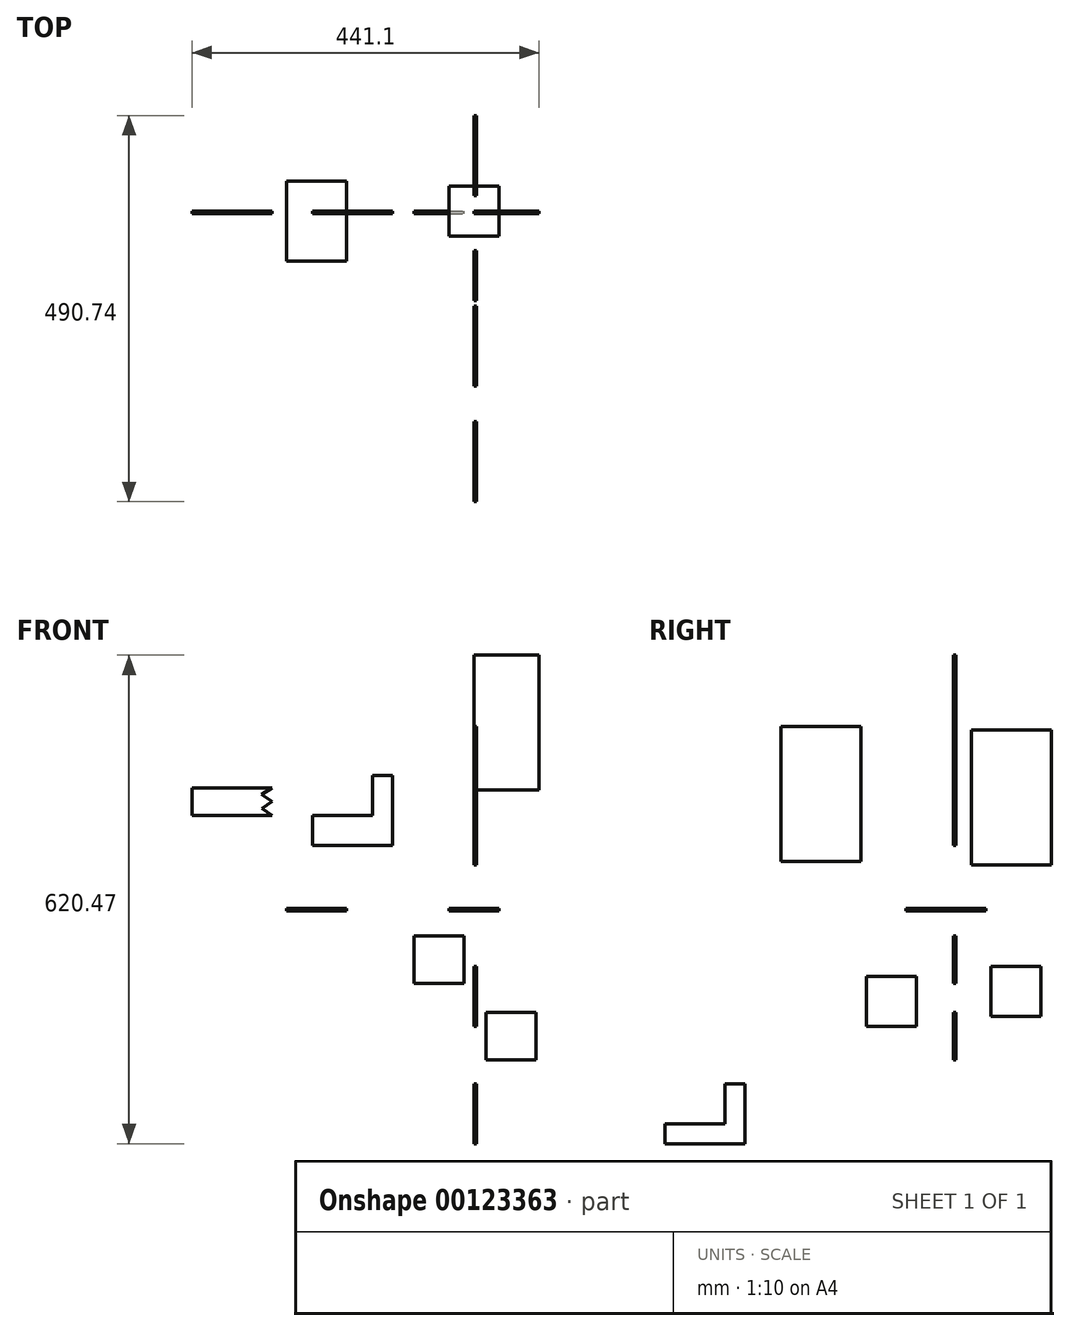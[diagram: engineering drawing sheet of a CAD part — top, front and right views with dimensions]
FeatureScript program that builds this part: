
annotation { "Feature Type Name" : "Feature", "Feature Type Description" : "" }
export const myFeature = defineFeature(function(context is Context, id is Id, definition is map)
    precondition{}
    {
        {
            var Q0;
            Q0=qCreatedBy(makeId("Top.planeOp"),FACE);
            var sketch = newSketch(context, id + "F0", { "sketchPlane" : qUnion([Q0])});
            skLineSegment(sketch, "E0.bottom", {"start": v(31.75, 31.75) * mm, "end": v(-31.75, 31.75) * mm});
            skLineSegment(sketch, "E0.top", {"start": v(31.75, -31.75) * mm, "end": v(-31.75, -31.75) * mm});
            skLineSegment(sketch, "E0.left", {"start": v(31.75, 31.75) * mm, "end": v(31.75, -31.75) * mm});
            skLineSegment(sketch, "E0.right", {"start": v(-31.75, 31.75) * mm, "end": v(-31.75, -31.75) * mm});
            skPoint(sketch, "E0.middle", {"position": v(0, 0) * mm});
            skLineSegment(sketch, "E1.bottom", {"start": v(-170.84, 127.02) * mm, "end": v(3.78, 127.02) * mm});
            skLineSegment(sketch, "E1.top", {"start": v(-170.84, 228.62) * mm, "end": v(3.78, 228.62) * mm});
            skLineSegment(sketch, "E1.left", {"start": v(-170.84, 127.02) * mm, "end": v(-170.84, 228.62) * mm});
            skLineSegment(sketch, "E1.right", {"start": v(3.78, 127.02) * mm, "end": v(3.78, 228.62) * mm});
            skPoint(sketch, "E1.middle", {"position": v(-83.53, 177.82) * mm});
            skLineSegment(sketch, "E2.bottom", {"start": v(0, -294.23) * mm, "end": v(-174.62, -294.23) * mm});
            skLineSegment(sketch, "E2.top", {"start": v(0, -192.63) * mm, "end": v(-174.63, -192.63) * mm});
            skLineSegment(sketch, "E2.left", {"start": v(0, -294.23) * mm, "end": v(0, -192.63) * mm});
            skLineSegment(sketch, "E2.right", {"start": v(-174.62, -294.23) * mm, "end": v(-174.63, -192.63) * mm});
            skPoint(sketch, "E2.middle", {"position": v(-87.31, -243.43) * mm});
            skLineSegment(sketch, "E3.bottom", {"start": v(-238.6, -63.17) * mm, "end": v(-162.4, -63.17) * mm});
            skLineSegment(sketch, "E3.top", {"start": v(-238.6, 38.43) * mm, "end": v(-162.4, 38.43) * mm});
            skLineSegment(sketch, "E3.left", {"start": v(-238.6, -63.17) * mm, "end": v(-238.6, 38.43) * mm});
            skLineSegment(sketch, "E3.right", {"start": v(-162.4, -63.17) * mm, "end": v(-162.4, 38.43) * mm});
            skPoint(sketch, "E3.middle", {"position": v(-200.5, -12.37) * mm});
            skSolve(sketch);
        }
        {
            var Q0;
            Q0=makeQuery(id+"F0.imprint","IMPRINT",FACE,{"disambiguationData":[TD([[makeQuery(id+"F0.imprint","IMPRINT",EDGE,{"derivedFrom":sQuery(id+"F0.wireOp",EDGE,"E0.bottom")}),1.0]])]});
            extrude(context, id + "F1", {"entities" : qUnion([Q0]), "depth" : 3.17 * mm});
        }
        {
            var Q0;
            Q0=qCreatedBy(makeId("Front.planeOp"),FACE);
            var sketch = newSketch(context, id + "F2", { "sketchPlane" : qUnion([Q0])});
            skLineSegment(sketch, "E4.bottom", {"start": v(-76.17, -31.8) * mm, "end": v(-12.67, -31.8) * mm});
            skLineSegment(sketch, "E4.top", {"start": v(-76.17, -92.13) * mm, "end": v(-12.67, -92.13) * mm});
            skLineSegment(sketch, "E4.left", {"start": v(-76.17, -31.8) * mm, "end": v(-76.17, -92.13) * mm});
            skLineSegment(sketch, "E4.right", {"start": v(-12.67, -31.8) * mm, "end": v(-12.67, -92.13) * mm});
            skPoint(sketch, "E4.middle", {"position": v(-44.42, -61.96) * mm});
            skLineSegment(sketch, "E5.bottom", {"start": v(14.92, -128.65) * mm, "end": v(78.42, -128.65) * mm});
            skLineSegment(sketch, "E5.top", {"start": v(14.92, -188.98) * mm, "end": v(78.42, -188.98) * mm});
            skLineSegment(sketch, "E5.left", {"start": v(14.92, -128.65) * mm, "end": v(14.92, -188.98) * mm});
            skLineSegment(sketch, "E5.right", {"start": v(78.42, -128.65) * mm, "end": v(78.42, -188.98) * mm});
            skPoint(sketch, "E5.middle", {"position": v(46.67, -158.82) * mm});
            skLineSegment(sketch, "E6.bottom", {"start": v(0, 324.95) * mm, "end": v(82.55, 324.95) * mm});
            skLineSegment(sketch, "E6.top", {"start": v(0, 153.5) * mm, "end": v(82.55, 153.5) * mm});
            skLineSegment(sketch, "E6.left", {"start": v(0, 324.95) * mm, "end": v(0, 153.5) * mm});
            skLineSegment(sketch, "E6.right", {"start": v(82.55, 324.95) * mm, "end": v(82.55, 153.5) * mm});
            skPoint(sketch, "E6.middle", {"position": v(41.28, 239.22) * mm});
            skLineSegment(sketch, "E7.bottom", {"start": v(-170.31, 227.53) * mm, "end": v(-271.91, 227.53) * mm});
            skLineSegment(sketch, "E7.top", {"start": v(-170.31, 265.63) * mm, "end": v(-271.91, 265.63) * mm});
            skLineSegment(sketch, "E7.left", {"start": v(-170.31, 227.53) * mm, "end": v(-170.31, 265.63) * mm});
            skLineSegment(sketch, "E7.right", {"start": v(-271.91, 227.53) * mm, "end": v(-271.91, 265.63) * mm});
            skPoint(sketch, "E7.middle", {"position": v(-221.11, 246.58) * mm});
            skLineSegment(sketch, "E8.bottom", {"start": v(-271.91, 227.53) * mm, "end": v(-246.51, 227.53) * mm});
            skLineSegment(sketch, "E8.top", {"start": v(-271.91, 316.43) * mm, "end": v(-246.51, 316.43) * mm});
            skLineSegment(sketch, "E8.left", {"start": v(-271.91, 227.53) * mm, "end": v(-271.91, 316.43) * mm});
            skLineSegment(sketch, "E8.right", {"start": v(-246.51, 227.53) * mm, "end": v(-246.51, 316.43) * mm});
            skLineSegment(sketch, "E9.bottom", {"start": v(-205.58, 121.73) * mm, "end": v(-103.98, 121.73) * mm});
            skLineSegment(sketch, "E9.top", {"start": v(-205.58, 83.63) * mm, "end": v(-103.98, 83.63) * mm});
            skLineSegment(sketch, "E9.left", {"start": v(-205.58, 121.73) * mm, "end": v(-205.58, 83.63) * mm});
            skLineSegment(sketch, "E9.right", {"start": v(-103.98, 121.73) * mm, "end": v(-103.98, 83.63) * mm});
            skPoint(sketch, "E9.middle", {"position": v(-154.78, 102.68) * mm});
            skLineSegment(sketch, "E10.bottom", {"start": v(-103.98, 83.63) * mm, "end": v(-129.38, 83.63) * mm});
            skLineSegment(sketch, "E10.top", {"start": v(-103.98, 172.53) * mm, "end": v(-129.38, 172.53) * mm});
            skLineSegment(sketch, "E10.left", {"start": v(-103.98, 83.63) * mm, "end": v(-103.98, 172.53) * mm});
            skLineSegment(sketch, "E10.right", {"start": v(-129.38, 83.63) * mm, "end": v(-129.38, 172.53) * mm});
            skLineSegment(sketch, "E11.bottom", {"start": v(-358.55, 156.27) * mm, "end": v(-256.95, 156.27) * mm});
            skLineSegment(sketch, "E11.top", {"start": v(-358.55, 121.7) * mm, "end": v(-256.95, 121.7) * mm});
            skLineSegment(sketch, "E11.left", {"start": v(-358.55, 156.27) * mm, "end": v(-358.55, 121.7) * mm});
            skLineSegment(sketch, "E11.right", {"start": v(-256.95, 156.27) * mm, "end": v(-256.95, 121.7) * mm});
            skPoint(sketch, "E11.middle", {"position": v(-307.75, 138.99) * mm});
            skLineSegment(sketch, "E12", {"start": v(-256.95, 121.7) * mm, "end": v(-269.2, 130.33) * mm});
            skLineSegment(sketch, "E13", {"start": v(-269.2, 130.33) * mm, "end": v(-256.95, 138.99) * mm});
            skLineSegment(sketch, "E14", {"start": v(-256.95, 138.99) * mm, "end": v(-269.2, 130.33) * mm});
            skLineSegment(sketch, "E15", {"start": v(-256.95, 156.27) * mm, "end": v(-270.41, 148.14) * mm});
            skLineSegment(sketch, "E16", {"start": v(-270.41, 148.14) * mm, "end": v(-256.95, 138.99) * mm});
            skSolve(sketch);
        }
        {
            var Q0;
            Q0=makeQuery(id+"F2.imprint","IMPRINT",FACE,{"disambiguationData":[TD([[makeQuery(id+"F2.imprint","IMPRINT",EDGE,{"derivedFrom":sQuery(id+"F2.wireOp",EDGE,"E4.bottom")}),-1.0]])]});
            extrude(context, id + "F3", {"entities" : qUnion([Q0]), "depth" : 3.17 * mm});
        }
        {
            var Q0;
            Q0=makeQuery(id+"F2.imprint","IMPRINT",FACE,{"disambiguationData":[TD([[makeQuery(id+"F2.imprint","IMPRINT",EDGE,{"derivedFrom":sQuery(id+"F2.wireOp",EDGE,"E5.bottom")}),-1.0]])]});
            extrude(context, id + "F4", {"entities" : qUnion([Q0]), "depth" : 3.17 * mm});
        }
        {
            var Q0;
            Q0=qCreatedBy(makeId("Right.planeOp"),FACE);
            var sketch = newSketch(context, id + "F5", { "sketchPlane" : qUnion([Q0])});
            skLineSegment(sketch, "E17.bottom", {"start": v(108.43, -133.8) * mm, "end": v(44.93, -133.8) * mm});
            skLineSegment(sketch, "E17.top", {"start": v(108.43, -70.3) * mm, "end": v(44.93, -70.3) * mm});
            skLineSegment(sketch, "E17.left", {"start": v(108.43, -133.8) * mm, "end": v(108.43, -70.3) * mm});
            skLineSegment(sketch, "E17.right", {"start": v(44.93, -133.8) * mm, "end": v(44.93, -70.3) * mm});
            skPoint(sketch, "E17.middle", {"position": v(76.68, -102.05) * mm});
            skLineSegment(sketch, "E18.bottom", {"start": v(-50.17, -146.33) * mm, "end": v(-113.67, -146.33) * mm});
            skLineSegment(sketch, "E18.top", {"start": v(-50.17, -82.83) * mm, "end": v(-113.67, -82.83) * mm});
            skLineSegment(sketch, "E18.left", {"start": v(-50.17, -146.33) * mm, "end": v(-50.17, -82.83) * mm});
            skLineSegment(sketch, "E18.right", {"start": v(-113.67, -146.33) * mm, "end": v(-113.67, -82.83) * mm});
            skPoint(sketch, "E18.middle", {"position": v(-81.92, -114.58) * mm});
            skLineSegment(sketch, "E19.bottom", {"start": v(-120.5, 234.76) * mm, "end": v(-222.1, 234.76) * mm});
            skLineSegment(sketch, "E19.top", {"start": v(-120.5, 63.3) * mm, "end": v(-222.1, 63.3) * mm});
            skLineSegment(sketch, "E19.left", {"start": v(-120.5, 234.76) * mm, "end": v(-120.5, 63.3) * mm});
            skLineSegment(sketch, "E19.right", {"start": v(-222.1, 234.76) * mm, "end": v(-222.1, 63.3) * mm});
            skPoint(sketch, "E19.middle", {"position": v(-171.3, 149.03) * mm});
            skLineSegment(sketch, "E20.bottom", {"start": v(121.62, 230.13) * mm, "end": v(20.02, 230.13) * mm});
            skLineSegment(sketch, "E20.top", {"start": v(121.62, 58.68) * mm, "end": v(20.02, 58.68) * mm});
            skLineSegment(sketch, "E20.left", {"start": v(121.62, 230.13) * mm, "end": v(121.62, 58.68) * mm});
            skLineSegment(sketch, "E20.right", {"start": v(20.02, 230.13) * mm, "end": v(20.02, 58.68) * mm});
            skPoint(sketch, "E20.middle", {"position": v(70.82, 144.4) * mm});
            skLineSegment(sketch, "E21.bottom", {"start": v(-402.14, -117.24) * mm, "end": v(-300.54, -117.24) * mm});
            skLineSegment(sketch, "E21.top", {"start": v(-402.14, -142.64) * mm, "end": v(-300.54, -142.64) * mm});
            skLineSegment(sketch, "E21.left", {"start": v(-402.14, -117.24) * mm, "end": v(-402.14, -142.64) * mm});
            skLineSegment(sketch, "E21.right", {"start": v(-300.54, -117.24) * mm, "end": v(-300.54, -142.64) * mm});
            skPoint(sketch, "E21.middle", {"position": v(-351.34, -129.94) * mm});
            skLineSegment(sketch, "E22.bottom", {"start": v(-369.12, -270.12) * mm, "end": v(-267.52, -270.12) * mm});
            skLineSegment(sketch, "E22.top", {"start": v(-369.12, -295.52) * mm, "end": v(-267.52, -295.52) * mm});
            skLineSegment(sketch, "E22.left", {"start": v(-369.12, -270.12) * mm, "end": v(-369.12, -295.52) * mm});
            skLineSegment(sketch, "E22.right", {"start": v(-267.52, -270.12) * mm, "end": v(-267.52, -295.52) * mm});
            skPoint(sketch, "E22.middle", {"position": v(-318.32, -282.82) * mm});
            skLineSegment(sketch, "E23.bottom", {"start": v(-267.52, -295.52) * mm, "end": v(-292.92, -295.52) * mm});
            skLineSegment(sketch, "E23.top", {"start": v(-267.52, -219.32) * mm, "end": v(-292.92, -219.32) * mm});
            skLineSegment(sketch, "E23.left", {"start": v(-267.52, -295.52) * mm, "end": v(-267.52, -219.32) * mm});
            skLineSegment(sketch, "E23.right", {"start": v(-292.92, -295.52) * mm, "end": v(-292.92, -219.32) * mm});
            skSolve(sketch);
        }
        {
            var Q0;
            Q0=makeQuery(id+"F5.imprint","IMPRINT",FACE,{"disambiguationData":[TD([[makeQuery(id+"F5.imprint","IMPRINT",EDGE,{"derivedFrom":sQuery(id+"F5.wireOp",EDGE,"E18.bottom")}),-1.0]])]});
            var Q1;
            Q1=makeQuery(id+"F5.imprint","IMPRINT",FACE,{"disambiguationData":[TD([[makeQuery(id+"F5.imprint","IMPRINT",EDGE,{"derivedFrom":sQuery(id+"F5.wireOp",EDGE,"E17.bottom")}),-1.0]])]});
            extrude(context, id + "F6", {"entities" : qUnion([Q0, Q1]), "depth" : 3.17 * mm});
        }
        {
            var Q0;
            Q0=makeQuery(id+"F0.imprint","IMPRINT",FACE,{"disambiguationData":[TD([[makeQuery(id+"F0.imprint","IMPRINT",EDGE,{"derivedFrom":sQuery(id+"F0.wireOp",EDGE,"E3.bottom")}),1.0]])]});
            extrude(context, id + "F7", {"entities" : qUnion([Q0]), "depth" : 3.17 * mm});
        }
        {
            var Q0;
            Q0=makeQuery(id+"F5.imprint","IMPRINT",FACE,{"disambiguationData":[TD([[makeQuery(id+"F5.imprint","IMPRINT",EDGE,{"derivedFrom":sQuery(id+"F5.wireOp",EDGE,"E20.bottom")}),1.0]])]});
            extrude(context, id + "F8", {"entities" : qUnion([Q0]), "depth" : 3.17 * mm});
        }
        {
            var Q0;
            Q0=makeQuery(id+"F5.imprint","IMPRINT",FACE,{"disambiguationData":[TD([[makeQuery(id+"F5.imprint","IMPRINT",EDGE,{"derivedFrom":sQuery(id+"F5.wireOp",EDGE,"E19.bottom")}),1.0]])]});
            extrude(context, id + "F9", {"entities" : qUnion([Q0]), "depth" : 3.17 * mm});
        }
        {
            var Q0;
            Q0=makeQuery(id+"F2.imprint","IMPRINT",FACE,{"disambiguationData":[TD([[makeQuery(id+"F2.imprint","IMPRINT",EDGE,{"derivedFrom":sQuery(id+"F2.wireOp",EDGE,"E6.bottom")}),-1.0]])]});
            extrude(context, id + "F10", {"entities" : qUnion([Q0]), "depth" : 3.17 * mm});
        }
        {
            var Q0;
            {var subQ4=sQuery(id+"F5.wireOp",EDGE,"E22.top");Q0=makeQuery(id+"F5.imprint","IMPRINT",FACE,{"disambiguationData":[TD([[makeQuery(id+"F5.imprint","IMPRINT",EDGE,{"derivedFrom":subQ4}),1.0]])]});}
            var Q1;
            {var subQ5=sQuery(id+"F5.wireOp",EDGE,"E23.bottom");Q1=makeQuery(id+"F5.imprint","IMPRINT",FACE,{"disambiguationData":[TD([[makeQuery(id+"F5.imprint","IMPRINT",EDGE,{"derivedFrom":subQ5}),-1.0]])]});}
            var Q2;
            {var subQ5=sQuery(id+"F5.wireOp",EDGE,"E23.top");Q2=makeQuery(id+"F5.imprint","IMPRINT",FACE,{"disambiguationData":[TD([[makeQuery(id+"F5.imprint","IMPRINT",EDGE,{"derivedFrom":subQ5}),1.0]])]});}
            extrude(context, id + "F11", {"entities" : qUnion([Q0, Q1, Q2]), "depth" : 3.17 * mm});
        }
        {
            var Q0;
            {var subQ5=sQuery(id+"F2.wireOp",EDGE,"E10.top");Q0=makeQuery(id+"F2.imprint","IMPRINT",FACE,{"disambiguationData":[TD([[makeQuery(id+"F2.imprint","IMPRINT",EDGE,{"derivedFrom":subQ5}),1.0]])]});}
            var Q1;
            {var subQ5=sQuery(id+"F2.wireOp",EDGE,"E10.bottom");Q1=makeQuery(id+"F2.imprint","IMPRINT",FACE,{"disambiguationData":[TD([[makeQuery(id+"F2.imprint","IMPRINT",EDGE,{"derivedFrom":subQ5}),-1.0]])]});}
            var Q2;
            {var subQ4=sQuery(id+"F2.wireOp",EDGE,"E9.top");Q2=makeQuery(id+"F2.imprint","IMPRINT",FACE,{"disambiguationData":[TD([[makeQuery(id+"F2.imprint","IMPRINT",EDGE,{"derivedFrom":subQ4}),1.0]])]});}
            extrude(context, id + "F12", {"entities" : qUnion([Q0, Q1, Q2]), "depth" : 3.17 * mm});
        }
        {
            var Q0;
            Q0=makeQuery(id+"F2.imprint","IMPRINT",FACE,{"disambiguationData":[TD([[makeQuery(id+"F2.imprint","IMPRINT",EDGE,{"derivedFrom":sQuery(id+"F2.wireOp",EDGE,"E11.bottom")}),-1.0]])]});
            extrude(context, id + "F13", {"entities" : qUnion([Q0]), "depth" : 3.17 * mm});
        }
    });
